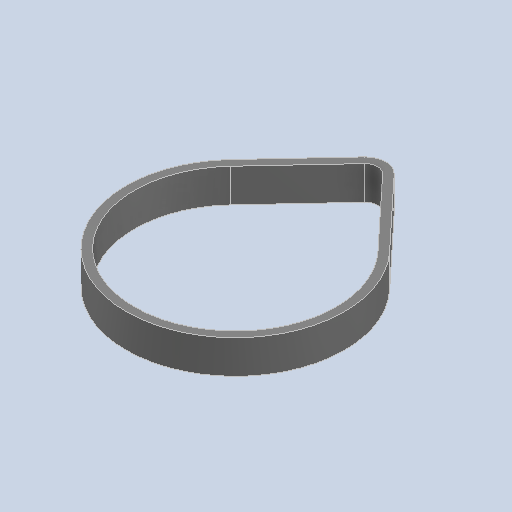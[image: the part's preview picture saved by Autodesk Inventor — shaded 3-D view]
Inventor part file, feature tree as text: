
AUTODESK INVENTOR PART (.ipt)
format: ipt  version: 2024.2 (Build 282272000, 272)  size: 97,792 bytes
history: native  units: in
note: dims shown in document units (in); Inventor stores cm internally (conversion verified against a paired STEP export)
features: extrude x1
ambient origin geometry x8: Origin, YZ Plane, XZ Plane, XY Plane, X Axis, Y Axis, Z Axis, Center Point
bodies: Solid1 (feature_tree)
feature tree (1):
  extrude  "Extrude-Thin1"  [1 undecoded]
note: 1 required parameter value undecoded (feature->parameter linkage not recoverable at this tier; creation-order binding heuristic only, values carry confidence <= 0.55)
